AUTODESK INVENTOR PART (.ipt)
format: ipt  version: 2015 (Build 190159000, 159)  size: 81,408 bytes
history: native  units: mm
features: sketch x2
ambient origin geometry x8: Origin, YZ Plane, XZ Plane, XY Plane, X Axis, Y Axis, Z Axis, Center Point
feature tree (2):
  sketch  "Sketch1"  dims[d0=210.0mm d1=35.0mm d2=5.0mm d3=285.0mm d4=22.0mm d5=10.0mm d8=1.0mm d9=1.0mm d10=3.0mm d11=3.0mm d12=3.0mm d13=3.0mm]
  sketch  "Sketch2"
